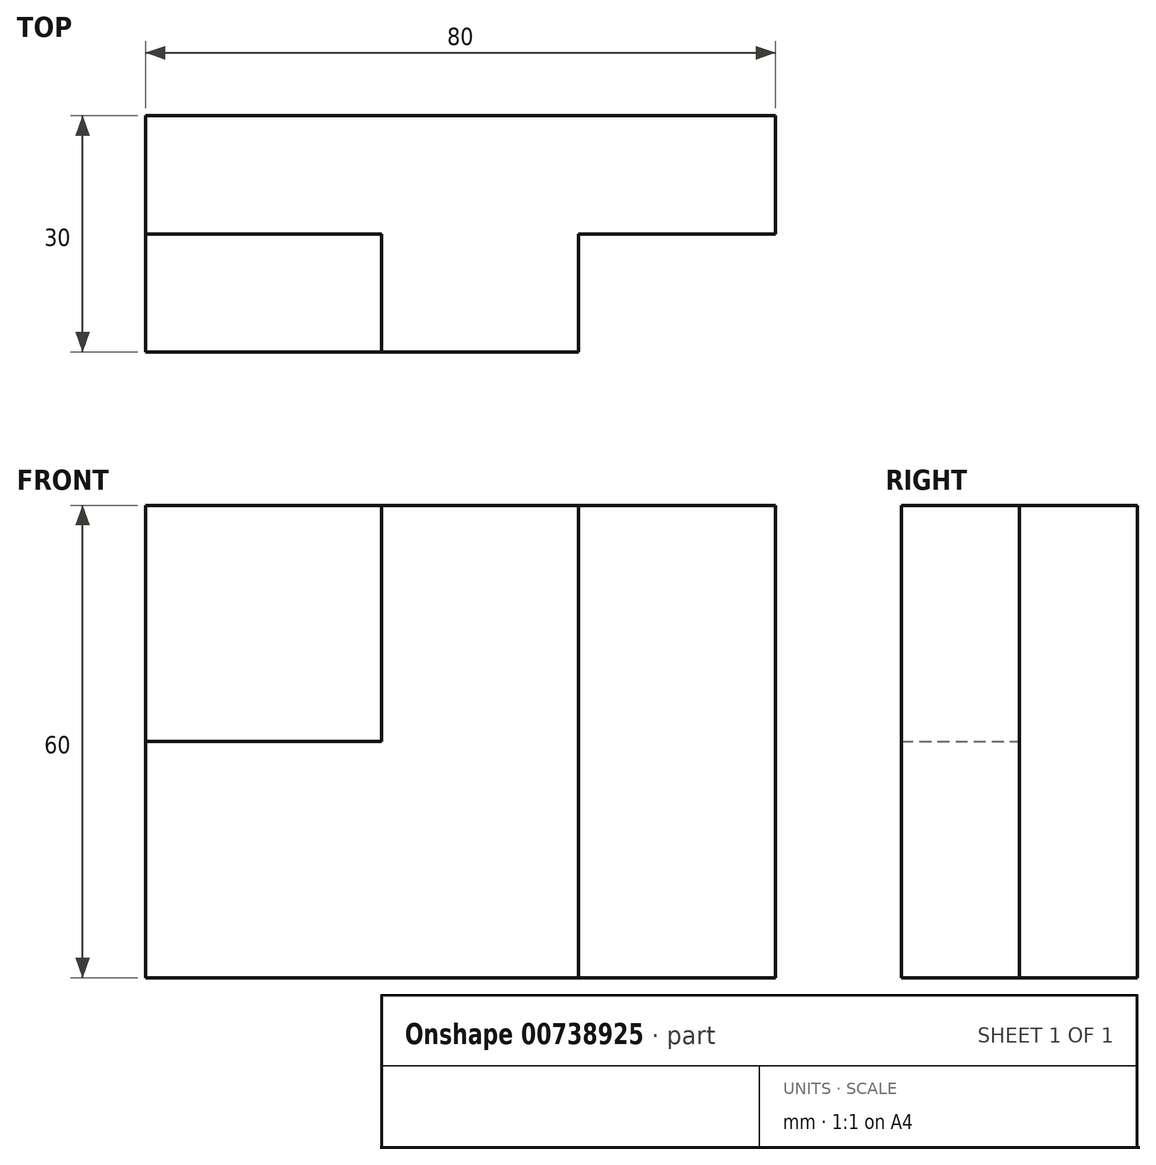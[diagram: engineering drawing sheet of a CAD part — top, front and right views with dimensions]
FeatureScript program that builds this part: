
annotation { "Feature Type Name" : "Feature", "Feature Type Description" : "" }
export const myFeature = defineFeature(function(context is Context, id is Id, definition is map)
    precondition{}
    {
        {
            var Q0;
            Q0=qCreatedBy(makeId("Front.planeOp"),FACE);
            var sketch = newSketch(context, id + "F0", { "sketchPlane" : qUnion([Q0])});
            skLineSegment(sketch, "E0", {"start": v(0, 0) * mm, "end": v(80, 0) * mm});
            skLineSegment(sketch, "E1", {"start": v(80, 0) * mm, "end": v(80, 60) * mm});
            skLineSegment(sketch, "E2", {"start": v(80, 60) * mm, "end": v(0, 60) * mm});
            skLineSegment(sketch, "E3", {"start": v(0, 60) * mm, "end": v(0, 0) * mm});
            skLineSegment(sketch, "E4", {"start": v(0, 30) * mm, "end": v(30, 30) * mm});
            skLineSegment(sketch, "E5", {"start": v(30, 30) * mm, "end": v(30, 60) * mm});
            skLineSegment(sketch, "E6", {"start": v(55, 60) * mm, "end": v(55, 0) * mm});
            skSolve(sketch);
        }
        {
            var Q0;
            {var subQ4=sQuery(id+"F0.wireOp",EDGE,"E4");Q0=makeQuery(id+"F0.imprint","IMPRINT",FACE,{"disambiguationData":[TD([[makeQuery(id+"F0.imprint","IMPRINT",EDGE,{"derivedFrom":subQ4}),1.0]])]});}
            var Q1;
            {var subQ0=sQuery(id+"F0.wireOp",EDGE,"E4");Q1=makeQuery(id+"F0.imprint","IMPRINT",FACE,{"disambiguationData":[TD([[makeQuery(id+"F0.imprint","IMPRINT",EDGE,{"derivedFrom":subQ0}),-1.0]])]});}
            var Q2;
            {var subQ0=sQuery(id+"F0.wireOp",EDGE,"E1");Q2=makeQuery(id+"F0.imprint","IMPRINT",FACE,{"disambiguationData":[TD([[makeQuery(id+"F0.imprint","IMPRINT",EDGE,{"derivedFrom":subQ0}),1.0]])]});}
            extrude(context, id + "F1", {"entities" : qUnion([Q0, Q1, Q2]), "depth" : 15 * mm, "offsetDistance" : 25 * mm});
        }
        {
            var Q0;
            {var subQ0=sQuery(id+"F0.wireOp",EDGE,"E4");Q0=makeQuery(id+"F0.imprint","IMPRINT",FACE,{"disambiguationData":[TD([[makeQuery(id+"F0.imprint","IMPRINT",EDGE,{"derivedFrom":subQ0}),-1.0]])]});}
            extrude(context, id + "F2", {"entities" : qUnion([Q0]), "operationType" : NewBodyOperationType.ADD, "depth" : 30 * mm, "offsetDistance" : 25 * mm});
        }
    });
